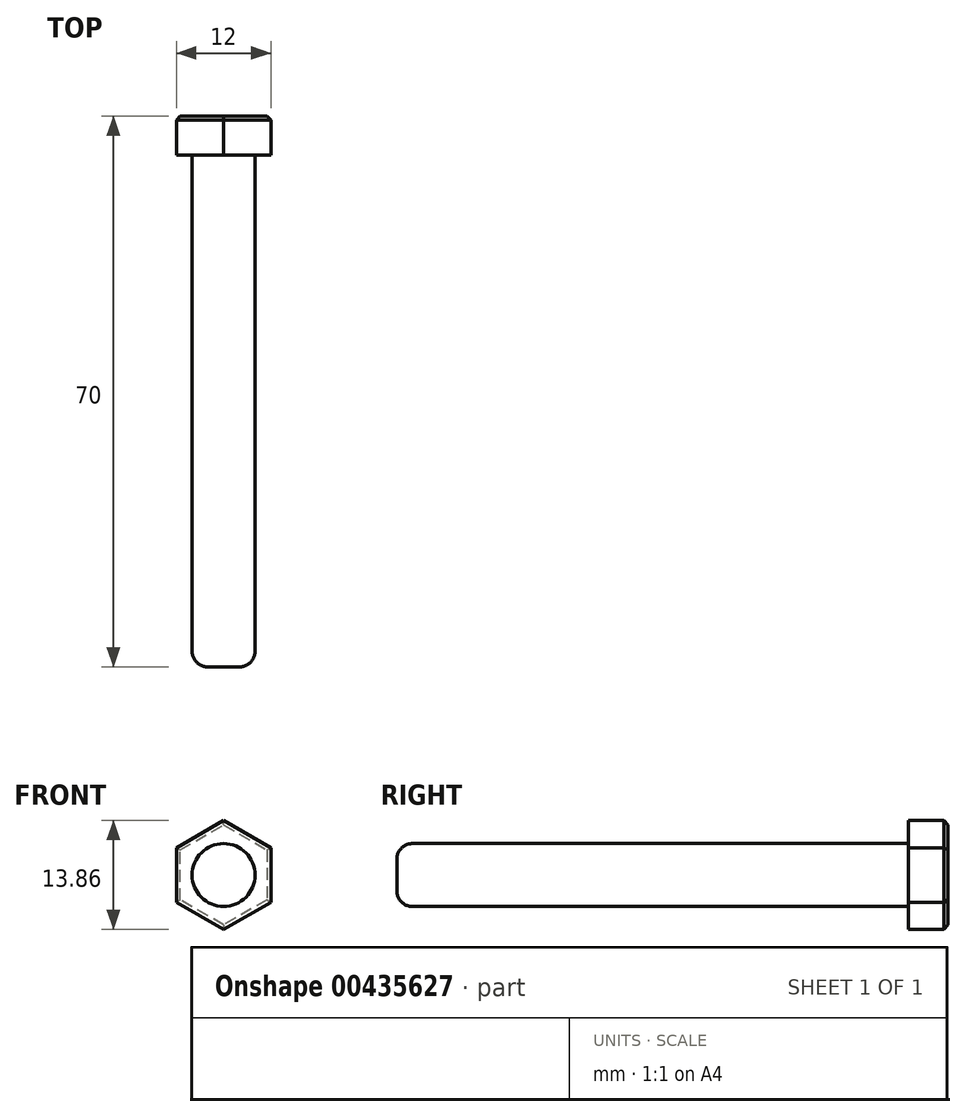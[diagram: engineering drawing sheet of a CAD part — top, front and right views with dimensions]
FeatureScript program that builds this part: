
annotation { "Feature Type Name" : "Feature", "Feature Type Description" : "" }
export const myFeature = defineFeature(function(context is Context, id is Id, definition is map)
    precondition{}
    {
        {
            var Q0;
            Q0=qCreatedBy(makeId("Front.planeOp"),FACE);
            var sketch = newSketch(context, id + "F0", { "sketchPlane" : qUnion([Q0])});
            skLineSegment(sketch, "E0", {"start": v(0, 5.58) * mm, "end": v(0, -11.02) * mm, "construction": true});
            skLineSegment(sketch, "E1", {"start": v(8.16, 0) * mm, "end": v(-10.4, 0) * mm, "construction": true});
            skLineSegment(sketch, "E2", {"start": v(-6, 3.56) * mm, "end": v(-6, -5.3) * mm, "construction": true});
            skLineSegment(sketch, "E3", {"start": v(6, 3.66) * mm, "end": v(6, -4.73) * mm, "construction": true});
            skLineSegment(sketch, "E4", {"start": v(0, 0) * mm, "end": v(-5.54, 9.6) * mm, "construction": true});
            skLineSegment(sketch, "E5", {"start": v(0, 0) * mm, "end": v(4.53, -7.85) * mm, "construction": true});
            skLineSegment(sketch, "E6", {"start": v(3.62, 6.27) * mm, "end": v(0, 0) * mm, "construction": true});
            skLineSegment(sketch, "E7", {"start": v(0, 0) * mm, "end": v(-4.28, -7.41) * mm, "construction": true});
            skLineSegment(sketch, "E8", {"start": v(3, 5.2) * mm, "end": v(9, 1.73) * mm, "construction": true});
            skLineSegment(sketch, "E9", {"start": v(3, 5.2) * mm, "end": v(-0.93, 7.47) * mm, "construction": true});
            skLineSegment(sketch, "E10", {"start": v(-3, 5.2) * mm, "end": v(0.64, 7.3) * mm, "construction": true});
            skLineSegment(sketch, "E11", {"start": v(-3, 5.2) * mm, "end": v(-6.22, 3.34) * mm, "construction": true});
            skLineSegment(sketch, "E12", {"start": v(-6, 3.46) * mm, "end": v(-6, 0) * mm});
            skLineSegment(sketch, "E13", {"start": v(-6, 3.46) * mm, "end": v(0, 6.93) * mm});
            skLineSegment(sketch, "E14", {"start": v(0, 6.93) * mm, "end": v(3, 5.2) * mm});
            skLineSegment(sketch, "E15", {"start": v(3, 5.2) * mm, "end": v(6, 3.46) * mm});
            skLineSegment(sketch, "E16", {"start": v(6, 3.46) * mm, "end": v(6, 0) * mm});
            skLineSegment(sketch, "E17.MirrorCS", {"start": v(-6, -3.46) * mm, "end": v(-6, 0) * mm});
            skLineSegment(sketch, "E18.MirrorCS", {"start": v(-6, -3.46) * mm, "end": v(0, -6.93) * mm});
            skLineSegment(sketch, "E19.MirrorCS", {"start": v(0, -6.93) * mm, "end": v(3, -5.2) * mm});
            skLineSegment(sketch, "E20.MirrorCS", {"start": v(3, -5.2) * mm, "end": v(6, -3.46) * mm});
            skLineSegment(sketch, "E21.MirrorCS", {"start": v(6, -3.46) * mm, "end": v(6, 0) * mm});
            skSolve(sketch);
        }
        {
            var Q0;
            Q0 = qSketchRegion(id + "F0", true);
            extrude(context, id + "F1", {"entities" : qUnion([Q0]), "oppositeDirection" : true, "depth" : 5 * mm});
        }
        {
            var Q0;
            Q0=makeQuery(id+"F1.opExtrude","CAP_FACE",FACE,{"disambiguationData":[OSD([sQuery(id+"F0.wireOp",EDGE,"E12"),sQuery(id+"F0.wireOp",EDGE,"E13"),sQuery(id+"F0.wireOp",EDGE,"E14"),sQuery(id+"F0.wireOp",EDGE,"E15"),sQuery(id+"F0.wireOp",EDGE,"E16"),sQuery(id+"F0.wireOp",EDGE,"E17.MirrorCS"),sQuery(id+"F0.wireOp",EDGE,"E18.MirrorCS"),sQuery(id+"F0.wireOp",EDGE,"E19.MirrorCS"),sQuery(id+"F0.wireOp",EDGE,"E20.MirrorCS"),sQuery(id+"F0.wireOp",EDGE,"E21.MirrorCS")])],"isStart":false});
            chamfer(context, id + "F2", {"entities" : qUnion([Q0]), "width" : 0.5 * mm, "tangentPropagation" : true});
        }
        {
            var Q0;
            Q0=makeQuery(id+"F1.opExtrude","CAP_FACE",FACE,{"disambiguationData":[OSD([sQuery(id+"F0.wireOp",EDGE,"E12"),sQuery(id+"F0.wireOp",EDGE,"E13"),sQuery(id+"F0.wireOp",EDGE,"E14"),sQuery(id+"F0.wireOp",EDGE,"E15"),sQuery(id+"F0.wireOp",EDGE,"E16"),sQuery(id+"F0.wireOp",EDGE,"E17.MirrorCS"),sQuery(id+"F0.wireOp",EDGE,"E18.MirrorCS"),sQuery(id+"F0.wireOp",EDGE,"E19.MirrorCS"),sQuery(id+"F0.wireOp",EDGE,"E20.MirrorCS"),sQuery(id+"F0.wireOp",EDGE,"E21.MirrorCS")])],"isStart":true});
            var sketch = newSketch(context, id + "F3", { "sketchPlane" : qUnion([Q0])});
            skCircle(sketch, "E22", {"center": v(0, 0) * mm, "radius": 4 * mm});
            skSolve(sketch);
        }
        {
            var Q0;
            Q0 = qSketchRegion(id + "F3", true);
            extrude(context, id + "F4", {"entities" : qUnion([Q0]), "operationType" : NewBodyOperationType.ADD, "depth" : 65 * mm});
        }
        {
            var Q0;
            Q0=makeQuery(id+"F4.opExtrude","CAP_EDGE",EDGE,{"disambiguationData":[OSD([sQuery(id+"F3.wireOp",EDGE,"E22")])],"isStart":false});
            fillet(context, id + "F5", {"entities" : qUnion([Q0]), "radius" : 2 * mm, "tangentPropagation" : true, "allowEdgeOverflow" : false});
        }
    });
